# Revit family: Tiefen_und_Plattener_Schlagspitze_für_Staberder_ST_und_BP
name_source: partatom
category: Generic Models
revit_build: Autodesk Revit 2015 (Build: 20140606_1530(x64)
units: mm (PartAtom-declared; Revit-internal decimal feet)

## types (2) — shared parameters
Manufacturer = OBO Bettermann
Material = Steel, Galvanized
URL = http://www.obo-bettermann.com

## per-type parameters (varying)
| type | Diameter dimesion | GTIN | Lenght 2 | Lenght3 | Manufacturer Art. No. | Outer Diameter Dimension |
| 1819 20BP | 6 mm  [stored 0.019685 ft] | 4012195242772 | 20 mm  [stored 0.0656168 ft] | 3 mm  [stored 0.00984252 ft] | 3041212 | 10 mm  [stored 0.0328084 ft] |
| 1819 25BP | 8 mm  [stored 0.0262467 ft] | 4012195242956 | 25 mm  [stored 0.082021 ft] | 5 mm  [stored 0.0164042 ft] | 3041956 | 13 mm |

note: column(s) folded — value = type name in every type: Article Type

note: [stored X ft] marks values corroborated as IEEE doubles in the binary element streams (Revit-internal decimal feet)

## geometry (parser evidence)
native form markers: Sweep x2
no freeform markers — native parametric forms only
